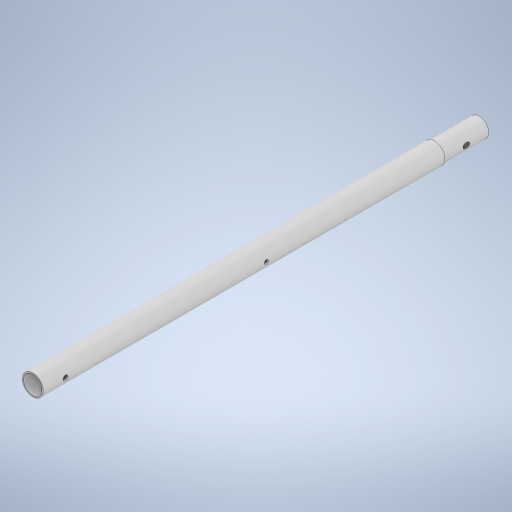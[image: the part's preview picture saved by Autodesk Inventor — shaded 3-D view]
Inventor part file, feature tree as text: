
AUTODESK INVENTOR PART (.ipt)
format: ipt  version: 2024 (Build 280153000, 153)  size: 303,616 bytes
history: native  units: mm
features: sketch x8, extrude x5, plane x4, hole x3
ambient origin geometry x8: Origin, YZ Plane, XZ Plane, XY Plane, X Axis, Y Axis, Z Axis, Center Point
bodies: Solid1 (feature_tree)
feature tree (20):
  extrude  "Extrusion1"  Depth=900.0mm TaperAngle=0.0deg
  extrude  "Extrusion2"  Depth=900.0mm TaperAngle=0.0deg
  extrude  "Extrusion3"  Depth=100.0mm TaperAngle=0.0deg
  extrude  "Extrusion4"  Depth=100.0mm TaperAngle=0.0deg
  plane  "Work Plane1"
  extrude  "Extrusion5"  Depth=11.0mm
  hole  "Hole1"  [1 undecoded]
  plane  "Work Plane2"
  plane  "Work Plane3"
  hole  "Hole3"  [1 undecoded]
  plane  "Work Plane4"
  hole  "Hole4"  [1 undecoded]
  sketch  "Sketch1"  dims[d0=47.0mm d1=900.0mm d2=0.0mm]
  sketch  "Sketch2"  dims[d3=41.0mm d4=900.0mm d5=0.0mm]
  sketch  "Sketch3"  dims[d6=43.0mm d7=100.0mm d8=0.0mm]
  sketch  "Sketch4"  dims[d9=41.0mm d10=100.0mm d11=0.0mm]
  sketch  "Sketch5"  dims[d12=23.5mm d13=11.0mm]
  sketch  "Sketch6"  dims[d14=48.0mm d15=11.0mm]
  sketch  "Sketch8"  dims[d16=52.0mm d17=11.0mm]
  sketch  "Sketch9"  dims[d18=47.0mm d19=0.0mm d20=11.0mm d21=50.0mm d22=11.0mm d23=6.0mm d24=4.0mm d25=2.0mm d26=90.0deg d27=47.0mm d28=0.0mm d29=23.25mm d39=30.0mm d40=9.0mm d41=500.0mm d42=9.0mm d43=6.0mm d44=4.0mm d45=2.0mm d46=90.0deg d47=50.0mm d48=0.0mm d49=-31.75mm d50=9.0mm d51=500.0mm d52=9.0mm d53=6.0mm d54=4.0mm d55=2.0mm d56=90.0deg d57=50.0mm d58=0.0mm]
note: 3 required parameter values undecoded (feature->parameter linkage not recoverable at this tier; creation-order binding heuristic only, values carry confidence <= 0.55)
